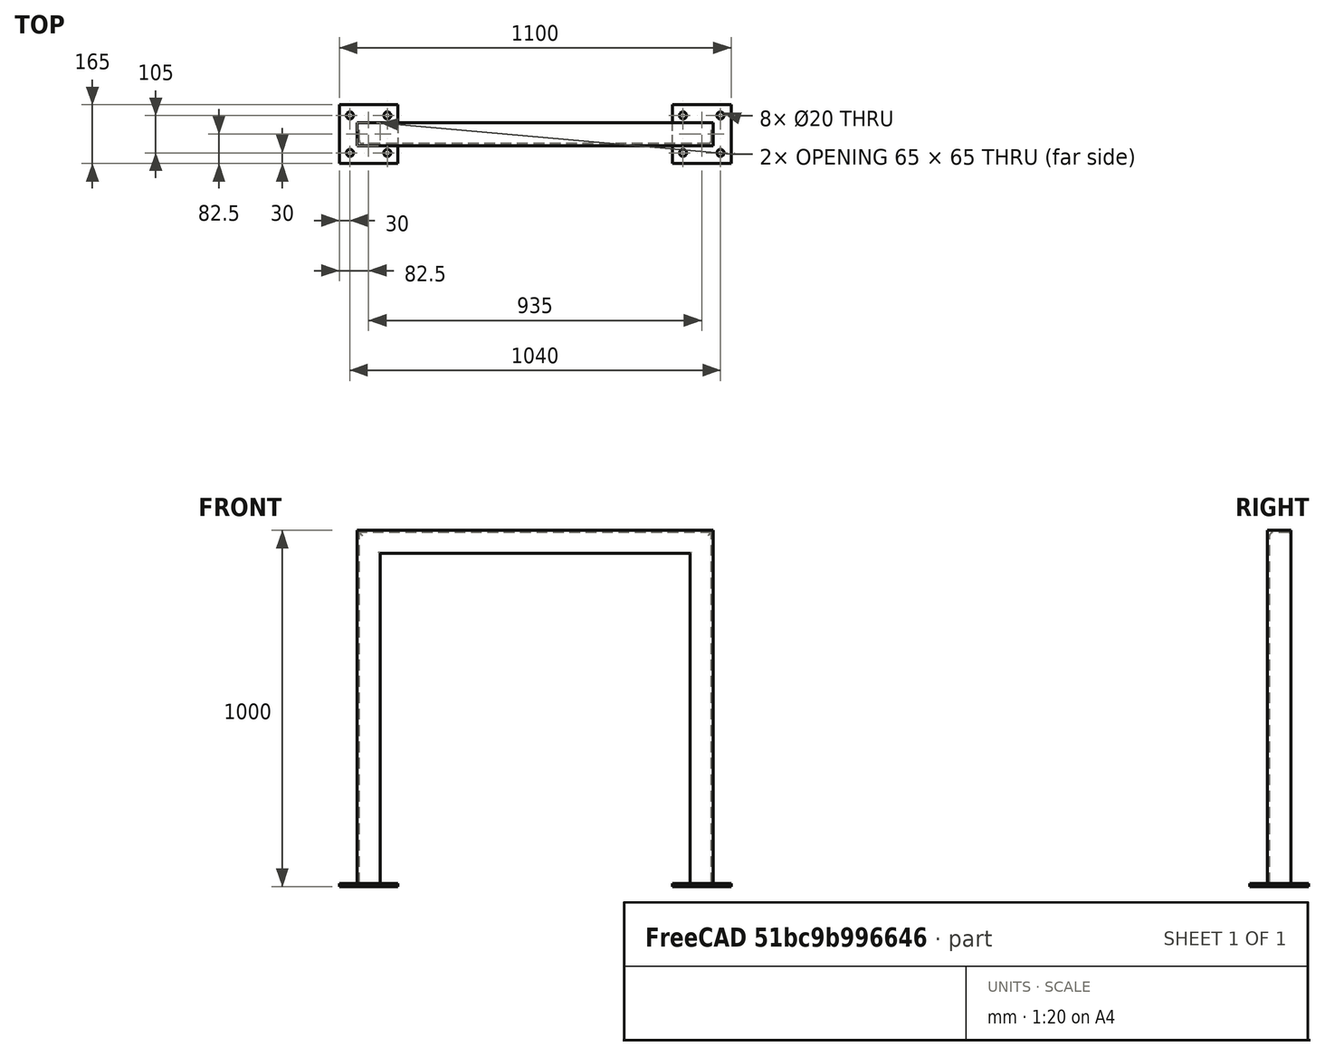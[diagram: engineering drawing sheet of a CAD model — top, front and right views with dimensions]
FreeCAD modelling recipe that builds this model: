
FCSTD DOCUMENT  (FreeCAD 0.21R30492 (Git))
Label: 05_Portal_Angle
License: All rights reserved
LicenseURL: http://en.wikipedia.org/wiki/All_rights_reserved
objects: Part::FeaturePython×3, Part::Extrusion×2, Part::MultiFuse×1
note: 6 computed .brp shape members not serialized (recipe doc carries the construction recipe); baked Part::Feature solids carry a one-line shape summary decoded from their .brp

FEATURE [Part::FeaturePython] s06L65x65x6  # WARN: FeaturePython — macro-defined, semantics opaque (R4)
  B = 85
  BasePlate = false
  H = 1000
  L1 = 1000
  Placement = pos=(-32.5,-32.5,0) rot=(0,0,1;0rad)
  W = 115
  key = 5
  key1 = 0
  size = 8
  t0 = 6
FEATURE [Part::FeaturePython] BasePlate  # WARN: FeaturePython — macro-defined, semantics opaque (R4)
  B = 165
  D = 20
  H = 165
  b1 = 30
  h1 = 30
  sface = 0
FEATURE [Part::FeaturePython] Clone  label="BasePlate001"  # Draft clone (typed FeaturePython)
  AttacherType = Attacher::AttachEngine3D
  Fuse = false
  Objects = -> [BasePlate]
  Placement = pos=(935,0,0) rot=(0,0,1;0rad)
  Scale = (1,1,1)
FEATURE [Part::Extrusion] Extrude
  Base = -> BasePlate
  Dir = (0,0,1)
  DirMode = 2
  FaceMakerClass = Part::FaceMakerBullseye
  LengthFwd = 9
  LengthRev = 0
  Solid = true
  Symmetric = false
FEATURE [Part::Extrusion] Extrude001
  Base = -> Clone
  Dir = (0,0,1)
  DirMode = 2
  FaceMakerClass = Part::FaceMakerBullseye
  LengthFwd = 9
  LengthRev = 0
  Solid = true
  Symmetric = false
FEATURE [Part::MultiFuse] Fusion  label="Portal_Angle"
  Shapes = -> [Extrude,Extrude001,s06L65x65x6]
